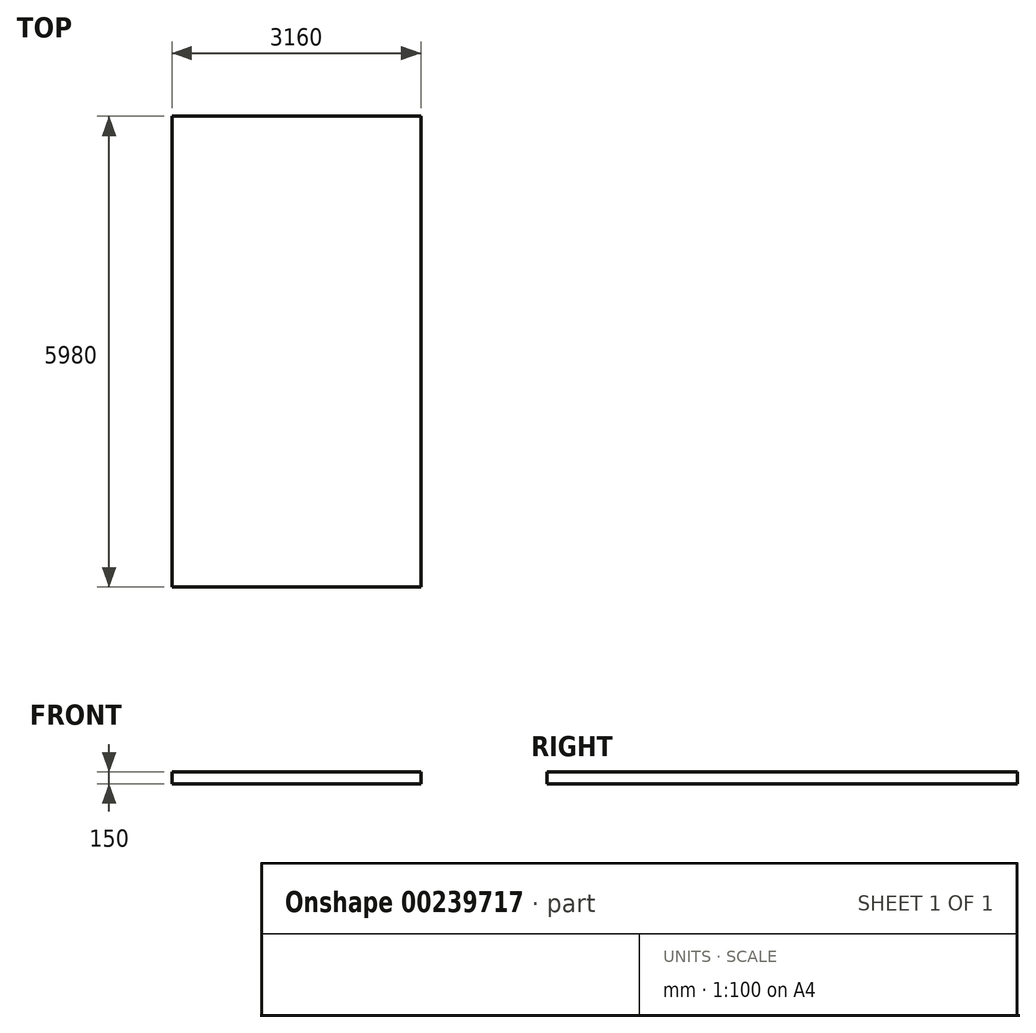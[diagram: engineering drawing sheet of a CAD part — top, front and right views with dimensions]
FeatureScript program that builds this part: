
annotation { "Feature Type Name" : "Feature", "Feature Type Description" : "" }
export const myFeature = defineFeature(function(context is Context, id is Id, definition is map)
    precondition{}
    {
        {
            var Q0;
            Q0=qCreatedBy(makeId("Top.planeOp"),FACE);
            var sketch = newSketch(context, id + "F0", { "sketchPlane" : qUnion([Q0])});
            skLineSegment(sketch, "E0.bottom", {"start": v(0, 0) * mm, "end": v(3160, 0) * mm});
            skLineSegment(sketch, "E0.top", {"start": v(0, 5980) * mm, "end": v(3160, 5980) * mm});
            skLineSegment(sketch, "E0.left", {"start": v(0, 0) * mm, "end": v(0, 5980) * mm});
            skLineSegment(sketch, "E0.right", {"start": v(3160, 0) * mm, "end": v(3160, 5980) * mm});
            skSolve(sketch);
        }
        {
            var Q0;
            Q0=makeQuery(id+"F0.imprint","IMPRINT",FACE,{"disambiguationData":[TD([[makeQuery(id+"F0.imprint","IMPRINT",EDGE,{"derivedFrom":sQuery(id+"F0.wireOp",EDGE,"E0.bottom")}),1.0]])]});
            extrude(context, id + "F1", {"entities" : qUnion([Q0]), "depth" : 150 * mm});
        }
    });
